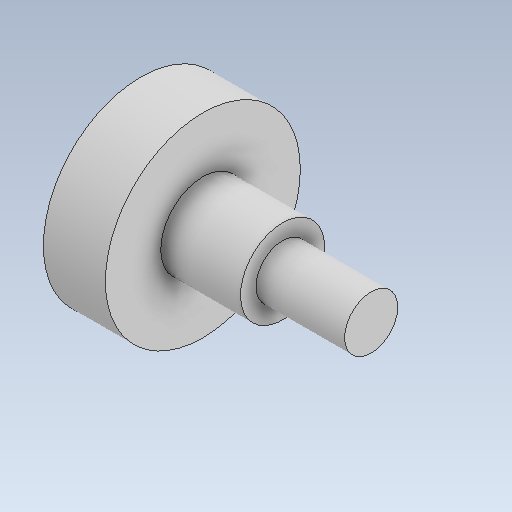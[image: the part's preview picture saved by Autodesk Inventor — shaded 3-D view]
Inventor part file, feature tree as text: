
AUTODESK INVENTOR PART (.ipt)
format: ipt  version: 2020 (Build 240168000, 168)  size: 122,368 bytes
history: native  units: mm
features: revolve x1, sketch x1
ambient origin geometry x8: Origin, YZ Plane, XZ Plane, XY Plane, X Axis, Y Axis, Z Axis, Center Point
bodies: Solid1 (feature_tree)
feature tree (2):
  revolve  "Revolution1"  Angle=90.0deg
  sketch  "Sketch1"  dims[d3=9.0mm d4=90.0deg d5=11.0mm d6=7.0mm d7=1.75mm d8=3.0mm d9=4.75mm]
